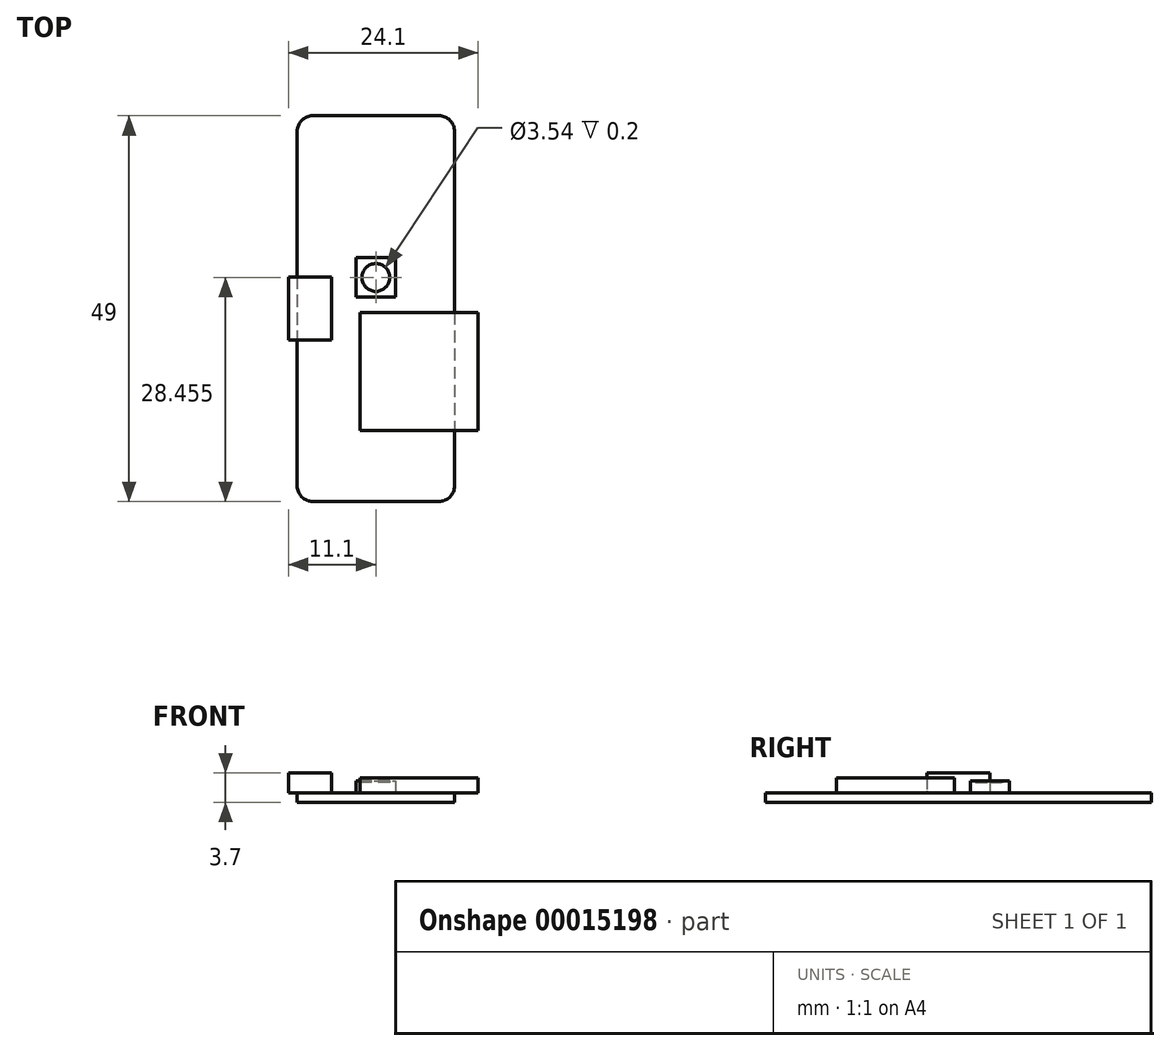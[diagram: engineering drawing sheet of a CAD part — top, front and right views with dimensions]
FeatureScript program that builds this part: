
annotation { "Feature Type Name" : "Feature", "Feature Type Description" : "" }
export const myFeature = defineFeature(function(context is Context, id is Id, definition is map)
    precondition{}
    {
        {
            var Q0;
            Q0=qCreatedBy(makeId("Top.planeOp"),FACE);
            var sketch = newSketch(context, id + "F0", { "sketchPlane" : qUnion([Q0])});
            skLineSegment(sketch, "E0.rect.bottom", {"start": v(10, 24.5) * mm, "end": v(-10, 24.5) * mm});
            skLineSegment(sketch, "E0.rect.top", {"start": v(10, -24.5) * mm, "end": v(-10, -24.5) * mm});
            skLineSegment(sketch, "E0.rect.left", {"start": v(10, 24.5) * mm, "end": v(10, -24.5) * mm});
            skLineSegment(sketch, "E0.rect.right", {"start": v(-10, 24.5) * mm, "end": v(-10, -24.5) * mm});
            skPoint(sketch, "E0.rect.middle", {"position": v(0, 0) * mm});
            skSolve(sketch);
        }
        {
            var Q0;
            Q0 = qSketchRegion(id + "F0", true);
            extrude(context, id + "F1", {"entities" : qUnion([Q0]), "depth" : 1.2 * mm});
        }
        {
            var Q0;
            Q0=makeQuery(id+"F1.opExtrude","SWEPT_EDGE",EDGE,{"disambiguationData":[OSD([sQuery(id+"F0.wireOp",EDGE,"E0.rect.top"),sQuery(id+"F0.wireOp",EDGE,"E0.rect.right")])]});
            var Q1;
            Q1=makeQuery(id+"F1.opExtrude","SWEPT_EDGE",EDGE,{"disambiguationData":[OSD([sQuery(id+"F0.wireOp",EDGE,"E0.rect.top"),sQuery(id+"F0.wireOp",EDGE,"E0.rect.left")])]});
            var Q2;
            Q2=makeQuery(id+"F1.opExtrude","SWEPT_EDGE",EDGE,{"disambiguationData":[OSD([sQuery(id+"F0.wireOp",EDGE,"E0.rect.bottom"),sQuery(id+"F0.wireOp",EDGE,"E0.rect.left")])]});
            var Q3;
            Q3=makeQuery(id+"F1.opExtrude","SWEPT_EDGE",EDGE,{"disambiguationData":[OSD([sQuery(id+"F0.wireOp",EDGE,"E0.rect.bottom"),sQuery(id+"F0.wireOp",EDGE,"E0.rect.right")])]});
            fillet(context, id + "F2", {"entities" : qUnion([Q0, Q1, Q2, Q3]), "radius" : 2 * mm, "tangentPropagation" : true, "allowEdgeOverflow" : false});
        }
        {
            var Q0;
            Q0=makeQuery(id+"F1.opExtrude","CAP_FACE",FACE,{"disambiguationData":[OSD([sQuery(id+"F0.wireOp",EDGE,"E0.rect.bottom"),sQuery(id+"F0.wireOp",EDGE,"E0.rect.top"),sQuery(id+"F0.wireOp",EDGE,"E0.rect.left"),sQuery(id+"F0.wireOp",EDGE,"E0.rect.right")])],"isStart":false});
            var sketch = newSketch(context, id + "F3", { "sketchPlane" : qUnion([Q0])});
            skLineSegment(sketch, "E1", {"start": v(0, 0) * mm, "end": v(-54.47, 0) * mm, "construction": true});
            skLineSegment(sketch, "E2.rect.bottom", {"start": v(-11.1, -4) * mm, "end": v(-5.6, -4) * mm});
            skLineSegment(sketch, "E2.rect.top", {"start": v(-11.1, 4) * mm, "end": v(-5.6, 4) * mm});
            skLineSegment(sketch, "E2.rect.left", {"start": v(-11.1, -4) * mm, "end": v(-11.1, 4) * mm});
            skLineSegment(sketch, "E2.rect.right", {"start": v(-5.6, -4) * mm, "end": v(-5.6, 4) * mm});
            skPoint(sketch, "E2.rect.middle", {"position": v(-8.35, 0) * mm});
            skSolve(sketch);
        }
        {
            var Q0;
            Q0 = qSketchRegion(id + "F3", true);
            extrude(context, id + "F4", {"entities" : qUnion([Q0]), "depth" : 2.5 * mm});
        }
        {
            var Q0;
            Q0=makeQuery(id+"F1.opExtrude","CAP_FACE",FACE,{"disambiguationData":[OSD([sQuery(id+"F0.wireOp",EDGE,"E0.rect.bottom"),sQuery(id+"F0.wireOp",EDGE,"E0.rect.top"),sQuery(id+"F0.wireOp",EDGE,"E0.rect.left"),sQuery(id+"F0.wireOp",EDGE,"E0.rect.right")])],"isStart":false});
            var sketch = newSketch(context, id + "F5", { "sketchPlane" : qUnion([Q0])});
            skLineSegment(sketch, "E3.bottom", {"start": v(13, -15.5) * mm, "end": v(-2, -15.5) * mm});
            skLineSegment(sketch, "E3.top", {"start": v(13, -0.5) * mm, "end": v(-2, -0.5) * mm});
            skLineSegment(sketch, "E3.left", {"start": v(13, -15.5) * mm, "end": v(13, -0.5) * mm});
            skLineSegment(sketch, "E3.right", {"start": v(-2, -15.5) * mm, "end": v(-2, -0.5) * mm});
            skSolve(sketch);
        }
        {
            var Q0;
            Q0 = qSketchRegion(id + "F5", true);
            extrude(context, id + "F6", {"entities" : qUnion([Q0]), "depth" : 1.9 * mm});
        }
        {
            var Q0;
            Q0=makeQuery(id+"F1.opExtrude","CAP_FACE",FACE,{"disambiguationData":[OSD([sQuery(id+"F0.wireOp",EDGE,"E0.rect.bottom"),sQuery(id+"F0.wireOp",EDGE,"E0.rect.top"),sQuery(id+"F0.wireOp",EDGE,"E0.rect.left"),sQuery(id+"F0.wireOp",EDGE,"E0.rect.right")])],"isStart":false});
            var sketch = newSketch(context, id + "F7", { "sketchPlane" : qUnion([Q0])});
            skLineSegment(sketch, "E4", {"start": v(0, 1.16) * mm, "end": v(0, 12.33) * mm, "construction": true});
            skLineSegment(sketch, "E5.rect.bottom", {"start": v(-2.5, 6.5) * mm, "end": v(2.5, 6.5) * mm});
            skLineSegment(sketch, "E5.rect.top", {"start": v(-2.5, 1.5) * mm, "end": v(2.5, 1.5) * mm});
            skLineSegment(sketch, "E5.rect.left", {"start": v(-2.5, 6.5) * mm, "end": v(-2.5, 1.5) * mm});
            skLineSegment(sketch, "E5.rect.right", {"start": v(2.5, 6.5) * mm, "end": v(2.5, 1.5) * mm});
            skPoint(sketch, "E5.rect.middle", {"position": v(0, 4) * mm});
            skCircle(sketch, "E6", {"center": v(0, 4) * mm, "radius": 1.75 * mm});
            skSolve(sketch);
        }
        {
            var Q0;
            Q0=makeQuery(id+"F7.imprint","IMPRINT",FACE,{"disambiguationData":[TD([[makeQuery(id+"F7.imprint","IMPRINT",EDGE,{"derivedFrom":sQuery(id+"F7.wireOp",EDGE,"E5.rect.bottom")}),-1.0]])]});
            var Q1;
            Q1=makeQuery(id+"F7.imprint","IMPRINT",FACE,{"disambiguationData":[TD([[makeQuery(id+"F7.imprint","IMPRINT",EDGE,{"derivedFrom":sQuery(id+"F7.wireOp",EDGE,"E6")}),1.0]])]});
            extrude(context, id + "F8", {"entities" : qUnion([Q0, Q1]), "depth" : 1.5 * mm});
        }
        {
            var Q0;
            Q0=makeQuery(id+"F8.opExtrude","CAP_FACE",FACE,{"disambiguationData":[OSD([sQuery(id+"F7.wireOp",EDGE,"E5.rect.bottom"),sQuery(id+"F7.wireOp",EDGE,"E5.rect.top"),sQuery(id+"F7.wireOp",EDGE,"E5.rect.left"),sQuery(id+"F7.wireOp",EDGE,"E5.rect.right")])],"isStart":false});
            var sketch = newSketch(context, id + "F9", { "sketchPlane" : qUnion([Q0])});
            skCircle(sketch, "E7", {"center": v(0, 3.96) * mm, "radius": 1.77 * mm});
            skSolve(sketch);
        }
        {
            var Q0;
            Q0 = qSketchRegion(id + "F9", true);
            extrude(context, id + "F10", {"entities" : qUnion([Q0]), "operationType" : NewBodyOperationType.REMOVE, "oppositeDirection" : true, "depth" : .2 * mm});
        }
    });
